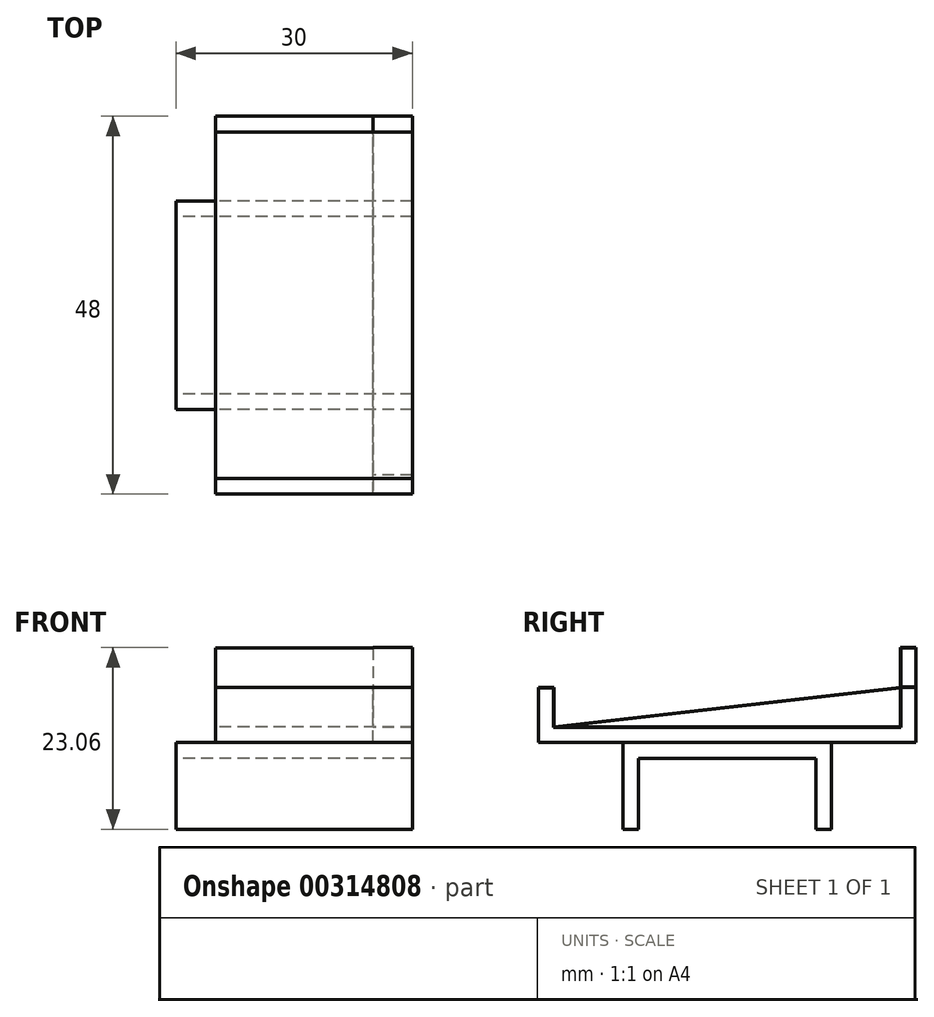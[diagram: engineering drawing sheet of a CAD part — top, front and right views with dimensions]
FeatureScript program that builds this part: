
annotation { "Feature Type Name" : "Feature", "Feature Type Description" : "" }
export const myFeature = defineFeature(function(context is Context, id is Id, definition is map)
    precondition{}
    {
        {
            var Q0;
            Q0=qCreatedBy(makeId("Right.planeOp"),FACE);
            var sketch = newSketch(context, id + "F0", { "sketchPlane" : qUnion([Q0])});
            skLineSegment(sketch, "E0.bottom", {"start": v(11.25, 4.5) * mm, "end": v(-11.25, 4.5) * mm});
            skLineSegment(sketch, "E0.top", {"start": v(13.25, -4.5) * mm, "end": v(11.25, -4.5) * mm});
            skLineSegment(sketch, "E0.left", {"start": v(11.25, 4.5) * mm, "end": v(11.25, -4.5) * mm});
            skLineSegment(sketch, "E0.right", {"start": v(-11.25, 4.5) * mm, "end": v(-11.25, -4.5) * mm});
            skPoint(sketch, "E0.middle", {"position": v(0, 0) * mm});
            skLineSegment(sketch, "E1.0", {"start": v(-13.25, 6.5) * mm, "end": v(-13.25, -4.5) * mm});
            skLineSegment(sketch, "E1.1", {"start": v(13.25, 6.5) * mm, "end": v(-13.25, 6.5) * mm});
            skLineSegment(sketch, "E1.2", {"start": v(13.25, 6.5) * mm, "end": v(13.25, -4.5) * mm});
            skLineSegment(sketch, "E2.trimOffspring", {"start": v(-11.25, -4.5) * mm, "end": v(-13.25, -4.5) * mm});
            skLineSegment(sketch, "E3", {"start": v(24, 6.5) * mm, "end": v(24, 13.5) * mm});
            skLineSegment(sketch, "E4", {"start": v(-24, 6.5) * mm, "end": v(24, 6.5) * mm});
            skLineSegment(sketch, "E5.0", {"start": v(-22, 8.5) * mm, "end": v(22, 8.5) * mm});
            skLineSegment(sketch, "E6.0", {"start": v(22, 13.5) * mm, "end": v(24, 13.5) * mm});
            skLineSegment(sketch, "E7.0", {"start": v(22, 8.5) * mm, "end": v(22, 13.5) * mm});
            skLineSegment(sketch, "E8.MirrorCS", {"start": v(-24, 6.5) * mm, "end": v(-24, 13.5) * mm});
            skLineSegment(sketch, "E9.MirrorCS", {"start": v(-22, 13.5) * mm, "end": v(-24, 13.5) * mm});
            skLineSegment(sketch, "E10.MirrorCS", {"start": v(-22, 8.5) * mm, "end": v(-22, 13.5) * mm});
            skLineSegment(sketch, "E11", {"start": v(-22, 8.5) * mm, "end": v(22, 13.5) * mm});
            skLineSegment(sketch, "E12.top", {"start": v(22, 18.5) * mm, "end": v(24, 18.5) * mm});
            skLineSegment(sketch, "E12.left", {"start": v(22, 13.5) * mm, "end": v(22, 18.5) * mm});
            skLineSegment(sketch, "E12.right", {"start": v(24, 13.5) * mm, "end": v(24, 18.5) * mm});
            skSolve(sketch);
        }
        {
            var Q0;
            Q0=makeQuery(id+"F0.imprint","IMPRINT",FACE,{"disambiguationData":[TD([[makeQuery(id+"F0.imprint","IMPRINT",EDGE,{"derivedFrom":sQuery(id+"F0.wireOp",EDGE,"E0.bottom")}),-1.0]])]});
            extrude(context, id + "F1", {"entities" : qUnion([Q0]), "endBound" : BoundingType.SYMMETRIC, "depth" : 30 * mm});
        }
        {
            var Q0;
            {var subQ2=sQuery(id+"F0.wireOp",EDGE,"E3");Q0=makeQuery(id+"F0.imprint","IMPRINT",FACE,{"disambiguationData":[TD([[makeQuery(id+"F0.imprint","IMPRINT",EDGE,{"derivedFrom":subQ2}),1.0]])]});}
            extrude(context, id + "F2", {"entities" : qUnion([Q0]), "operationType" : NewBodyOperationType.ADD, "endBound" : BoundingType.SYMMETRIC, "depth" : 20 * mm});
        }
        {
            var Q0;
            Q0=makeQuery(id+"F2.opExtrude","CAP_FACE",FACE,{"disambiguationData":[OSD([sQuery(id+"F0.wireOp",EDGE,"E3"),sQuery(id+"F0.wireOp",EDGE,"E4"),sQuery(id+"F0.wireOp",EDGE,"E5.0"),sQuery(id+"F0.wireOp",EDGE,"E6.0"),sQuery(id+"F0.wireOp",EDGE,"E7.0"),sQuery(id+"F0.wireOp",EDGE,"E8.MirrorCS"),sQuery(id+"F0.wireOp",EDGE,"E9.MirrorCS"),sQuery(id+"F0.wireOp",EDGE,"E10.MirrorCS")])],"isStart":false});
            var sketch = newSketch(context, id + "F3", { "sketchPlane" : qUnion([Q0])});
            skLineSegment(sketch, "E13", {"start": v(-24, 13.5) * mm, "end": v(-22, 13.5) * mm});
            skLineSegment(sketch, "E14", {"start": v(-22, 13.5) * mm, "end": v(-22, 8.5) * mm});
            skLineSegment(sketch, "E15", {"start": v(-22, 8.5) * mm, "end": v(22, 8.5) * mm});
            skLineSegment(sketch, "E16", {"start": v(22, 8.5) * mm, "end": v(22, 8.5) * mm});
            skLineSegment(sketch, "E17", {"start": v(24, 6.5) * mm, "end": v(24, 6.5) * mm});
            skLineSegment(sketch, "E18", {"start": v(24, 6.5) * mm, "end": v(-24, 6.5) * mm});
            skLineSegment(sketch, "E19", {"start": v(-24, 6.5) * mm, "end": v(-24, 13.5) * mm});
            skLineSegment(sketch, "E20.0", {"start": v(-22.05, 8.45) * mm, "end": v(22.05, 8.45) * mm});
            skLineSegment(sketch, "E20.1", {"start": v(-22.05, 13.45) * mm, "end": v(-22.05, 8.45) * mm});
            skLineSegment(sketch, "E20.3", {"start": v(-23.95, 13.45) * mm, "end": v(-22.05, 13.45) * mm});
            skLineSegment(sketch, "E20.6", {"start": v(23.95, 6.55) * mm, "end": v(-23.95, 6.55) * mm});
            skLineSegment(sketch, "E20.7", {"start": v(-23.95, 6.55) * mm, "end": v(-23.95, 13.45) * mm});
            skLineSegment(sketch, "E21", {"start": v(24, 6.5) * mm, "end": v(24, 13.5) * mm});
            skLineSegment(sketch, "E22", {"start": v(23.95, 13.5) * mm, "end": v(22.05, 13.5) * mm});
            skLineSegment(sketch, "E23", {"start": v(-22, 8.5) * mm, "end": v(22, 13.5) * mm});
            skLineSegment(sketch, "E24", {"start": v(22, 18.56) * mm, "end": v(24, 18.56) * mm});
            skLineSegment(sketch, "E25", {"start": v(24, 18.56) * mm, "end": v(24, 13.5) * mm});
            skLineSegment(sketch, "E26", {"start": v(22, 18.56) * mm, "end": v(22, 13.5) * mm});
            skLineSegment(sketch, "E27.0", {"start": v(22.05, 18.51) * mm, "end": v(22.05, 13.56) * mm});
            skLineSegment(sketch, "E28.0", {"start": v(22.05, 13.56) * mm, "end": v(23.95, 13.56) * mm});
            skLineSegment(sketch, "E29.0", {"start": v(23.95, 18.51) * mm, "end": v(23.95, 13.56) * mm});
            skLineSegment(sketch, "E30.0", {"start": v(22.05, 18.51) * mm, "end": v(23.95, 18.51) * mm});
            skLineSegment(sketch, "E31.0", {"start": v(23.95, 6.55) * mm, "end": v(23.95, 13.5) * mm});
            skLineSegment(sketch, "E32.0", {"start": v(-21.56, 8.5) * mm, "end": v(22, 13.45) * mm});
            skLineSegment(sketch, "E33", {"start": v(22.05, 8.45) * mm, "end": v(22.05, 13.5) * mm});
            skLineSegment(sketch, "E34", {"start": v(22, 13.45) * mm, "end": v(22, 8.5) * mm});
            skSolve(sketch);
        }
        {
            var Q0;
            Q0=makeQuery(id+"F3.imprint","IMPRINT",FACE,{"disambiguationData":[TD([[makeQuery(id+"F3.imprint","IMPRINT",EDGE,{"derivedFrom":sQuery(id+"F3.wireOp",EDGE,"E13")}),1.0]])]});
            extrude(context, id + "F4", {"entities" : qUnion([Q0]), "operationType" : NewBodyOperationType.ADD, "depth" : 5 * mm});
        }
        {
            var Q0;
            Q0=makeQuery(id+"F0.imprint","IMPRINT",FACE,{"disambiguationData":[TD([[makeQuery(id+"F0.imprint","IMPRINT",EDGE,{"derivedFrom":sQuery(id+"F0.wireOp",EDGE,"E6.0")}),1.0]])]});
            extrude(context, id + "F5", {"entities" : qUnion([Q0]), "operationType" : NewBodyOperationType.ADD, "endBound" : BoundingType.SYMMETRIC, "depth" : 20 * mm});
        }
        {
            var Q0;
            Q0=makeQuery(id+"F0.imprint","IMPRINT",FACE,{"disambiguationData":[TD([[makeQuery(id+"F0.imprint","IMPRINT",EDGE,{"derivedFrom":sQuery(id+"F0.wireOp",EDGE,"E5.0")}),1.0]])]});
            extrude(context, id + "F6", {"entities" : qUnion([Q0]), "operationType" : NewBodyOperationType.ADD, "endBound" : BoundingType.SYMMETRIC, "depth" : 20 * mm});
        }
        {
            var Q0;
            {var subQ2=sQuery(id+"F3.wireOp",EDGE,"E22");Q0=makeQuery(id+"F3.imprint","IMPRINT",FACE,{"disambiguationData":[TD([[makeQuery(id+"F3.imprint","IMPRINT",EDGE,{"derivedFrom":subQ2}),1.0]])]});}
            var Q1;
            {var subQ0=sQuery(id+"F3.wireOp",EDGE,"E23");Q1=makeQuery(id+"F3.imprint","IMPRINT",FACE,{"disambiguationData":[TD([[makeQuery(id+"F3.imprint","IMPRINT",EDGE,{"derivedFrom":subQ0}),-1.0]])]});}
            extrude(context, id + "F7", {"entities" : qUnion([Q0, Q1]), "operationType" : NewBodyOperationType.ADD, "depth" : 5 * mm});
        }
    });
